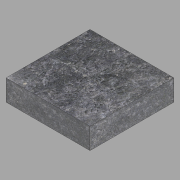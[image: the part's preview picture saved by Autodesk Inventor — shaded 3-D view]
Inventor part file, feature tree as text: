
AUTODESK INVENTOR PART (.ipt)
format: ipt  version: 2022.2 (Build 262287000, 287)  size: 116,736 bytes
history: native  units: in
note: dims shown in document units (in); Inventor stores cm internally (conversion verified against a paired STEP export)
features: extrude x1, sketch x1
ambient origin geometry x8: Origin, YZ Plane, XZ Plane, XY Plane, X Axis, Y Axis, Z Axis, Center Point
bodies: Solid1 (feature_tree)
feature tree (2):
  extrude  "Extrusion1"  Depth=8.0in
  sketch  "Sketch1"  dims[d0=8.0in d1=8.0in d2=2.0in d3=0.0in]
